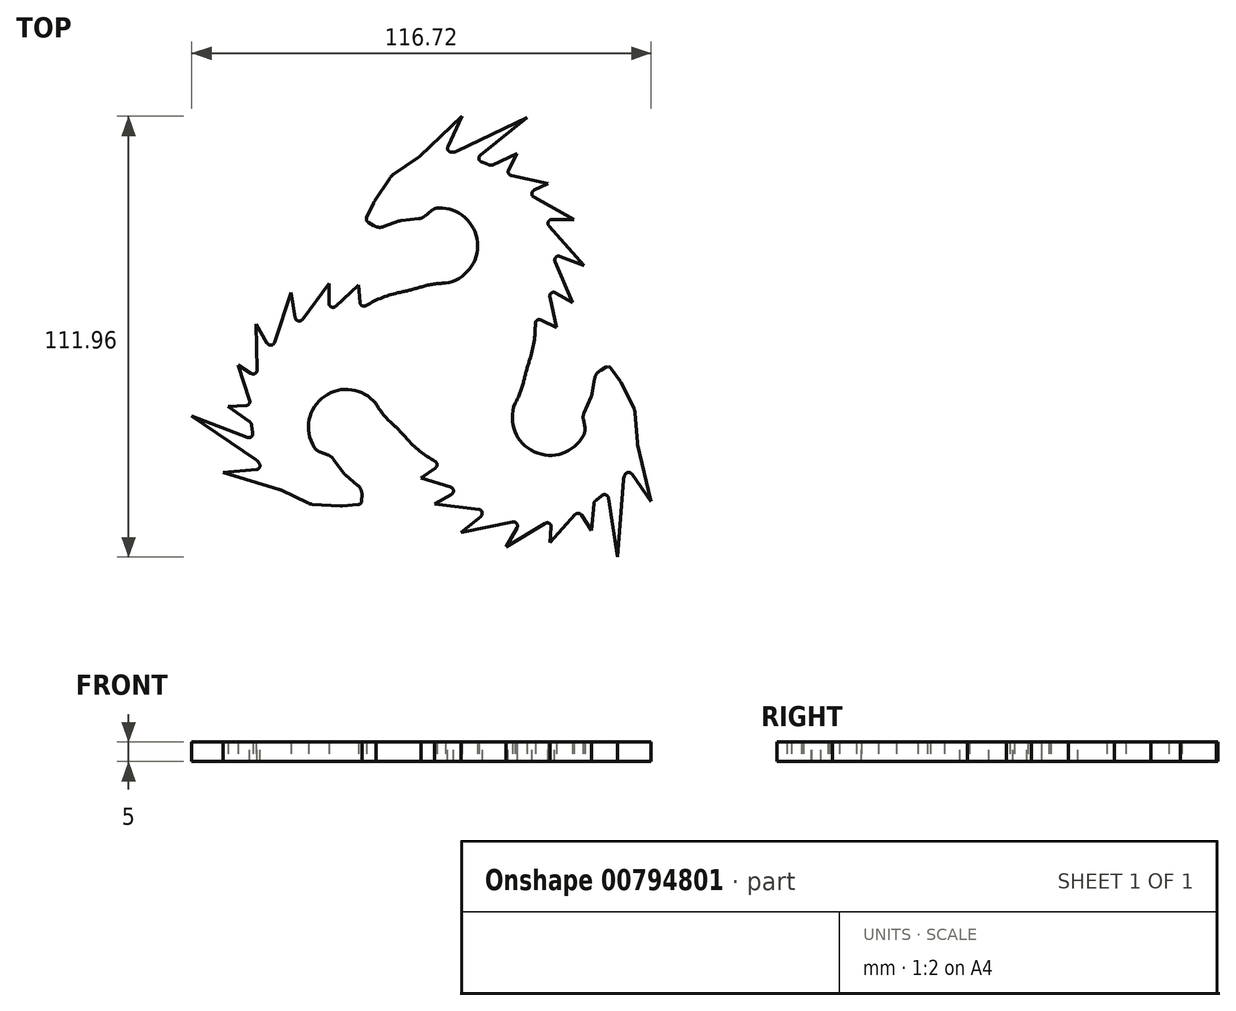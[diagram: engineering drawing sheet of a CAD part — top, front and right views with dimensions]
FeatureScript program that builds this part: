
annotation { "Feature Type Name" : "Feature", "Feature Type Description" : "" }
export const myFeature = defineFeature(function(context is Context, id is Id, definition is map)
    precondition{}
    {
        {
            var Q0;
            Q0=qCreatedBy(makeId("Top.planeOp"),FACE);
            var sketch = newSketch(context, id + "F0", { "sketchPlane" : qUnion([Q0])});
            skCircle(sketch, "E0", {"center": v(0, 0) * mm, "radius": 14.28 * mm});
            skCircle(sketch, "E1", {"center": v(0, 0) * mm, "radius": 20.4 * mm});
            skArc(sketch, "E2", {"start": v(0, 20.4) * mm, "mid": v(8.14, 30.78) * mm, "end": v(-1.75, 39.51) * mm});
            skArc(sketch, "E3", {"start": v(19.07, 7.24) * mm, "mid": v(26.13, 32.87) * mm, "end": v(7.42, 51.76) * mm});
            skLineSegment(sketch, "E4", {"start": v(7.42, 51.76) * mm, "end": v(20.67, 62.5) * mm});
            skLineSegment(sketch, "E5", {"start": v(20.67, 62.5) * mm, "end": v(2.99, 53.95) * mm});
            skLineSegment(sketch, "E6", {"start": v(1.68, 53.66) * mm, "end": v(0, 53.66) * mm});
            skLineSegment(sketch, "E7", {"start": v(-6.98, 52.26) * mm, "end": v(-13.25, 47.99) * mm});
            skLineSegment(sketch, "E8", {"start": v(-20.36, 36.3) * mm, "end": v(-18.24, 40.82) * mm});
            skLineSegment(sketch, "E9", {"start": v(-18.02, 41.22) * mm, "end": v(-14.05, 47.17) * mm});
            skLineSegment(sketch, "E10", {"start": v(-3.58, 38.81) * mm, "end": v(-5.17, 37.47) * mm});
            skLineSegment(sketch, "E11", {"start": v(-6.77, 36.79) * mm, "end": v(-11.2, 36.3) * mm});
            skLineSegment(sketch, "E12", {"start": v(-11.89, 36.13) * mm, "end": v(-15.65, 34.77) * mm});
            skLineSegment(sketch, "E13", {"start": v(-18.22, 35.01) * mm, "end": v(-20.36, 36.3) * mm});
            skLineSegment(sketch, "E14", {"start": v(0, 53.66) * mm, "end": v(4.26, 62.8) * mm});
            skLineSegment(sketch, "E15", {"start": v(4.26, 62.8) * mm, "end": v(-6.61, 52.56) * mm});
            skLineSegment(sketch, "E16", {"start": v(15.49, 48.02) * mm, "end": v(26.04, 45.77) * mm});
            skLineSegment(sketch, "E17", {"start": v(26.04, 45.77) * mm, "end": v(20.8, 43.18) * mm});
            skLineSegment(sketch, "E18", {"start": v(20.8, 43.18) * mm, "end": v(32.67, 36.61) * mm});
            skLineSegment(sketch, "E19", {"start": v(32.67, 36.61) * mm, "end": v(24.84, 36.61) * mm});
            skLineSegment(sketch, "E20", {"start": v(24.84, 36.61) * mm, "end": v(35.2, 24.93) * mm});
            skLineSegment(sketch, "E21", {"start": v(35.2, 24.93) * mm, "end": v(26.92, 28.04) * mm});
            skLineSegment(sketch, "E22", {"start": v(26.92, 28.04) * mm, "end": v(32.35, 15.47) * mm});
            skLineSegment(sketch, "E23", {"start": v(32.35, 15.47) * mm, "end": v(26.04, 19.1) * mm});
            skLineSegment(sketch, "E24", {"start": v(26.04, 19.1) * mm, "end": v(28.25, 9.15) * mm});
            skLineSegment(sketch, "E25", {"start": v(28.25, 9.15) * mm, "end": v(22.76, 11.77) * mm});
            skLineSegment(sketch, "E26", {"start": v(11.52, 50.27) * mm, "end": v(18.15, 53.34) * mm});
            skPoint(sketch, "E26.startSnap0", {"position": v(11.52, 58.07) * mm});
            skLineSegment(sketch, "E27", {"start": v(18.15, 53.34) * mm, "end": v(15.49, 48.02) * mm});
            skPoint(sketch, "E28.visualSharp", {"position": v(-17, 34.28) * mm});
            skArc(sketch, "E28.filletArc", {"start": v(-18.22, 35.01) * mm, "mid": v(-16.96, 34.6) * mm, "end": v(-15.65, 34.77) * mm});
            skPoint(sketch, "E29.visualSharp", {"position": v(-11.55, 36.26) * mm});
            skArc(sketch, "E29.filletArc", {"start": v(-11.2, 36.3) * mm, "mid": v(-11.54, 36.24) * mm, "end": v(-11.89, 36.13) * mm});
            skPoint(sketch, "E30.visualSharp", {"position": v(-5.87, 36.89) * mm});
            skArc(sketch, "E30.filletArc", {"start": v(-6.77, 36.79) * mm, "mid": v(-5.92, 37.01) * mm, "end": v(-5.17, 37.47) * mm});
            skPoint(sketch, "E31.visualSharp", {"position": v(-2.87, 39.41) * mm});
            skArc(sketch, "E31.filletArc", {"start": v(-1.75, 39.51) * mm, "mid": v(-2.72, 39.32) * mm, "end": v(-3.58, 38.81) * mm});
            skPoint(sketch, "E32.visualSharp", {"position": v(-18.15, 41.03) * mm});
            skArc(sketch, "E32.filletArc", {"start": v(-18.02, 41.22) * mm, "mid": v(-18.14, 41.03) * mm, "end": v(-18.24, 40.82) * mm});
            skPoint(sketch, "E33.visualSharp", {"position": v(-13.73, 47.66) * mm});
            skArc(sketch, "E33.filletArc", {"start": v(-13.25, 47.99) * mm, "mid": v(-13.69, 47.62) * mm, "end": v(-14.05, 47.17) * mm});
            skPoint(sketch, "E34.visualSharp", {"position": v(-6.79, 52.4) * mm});
            skArc(sketch, "E34.filletArc", {"start": v(-6.98, 52.26) * mm, "mid": v(-6.8, 52.4) * mm, "end": v(-6.61, 52.56) * mm});
            skPoint(sketch, "E35.visualSharp", {"position": v(2.37, 53.66) * mm});
            skArc(sketch, "E35.filletArc", {"start": v(1.68, 53.66) * mm, "mid": v(2.35, 53.73) * mm, "end": v(2.99, 53.95) * mm});
            skArc(sketch, "E36", {"start": v(20.32, -1.85) * mm, "mid": v(22.4, 4.8) * mm, "end": v(22.76, 11.77) * mm});
            skSolve(sketch);
        }
        {
            var Q0;
            Q0=qSketchRegion(id+"F0",true);
            extrude(context, id + "F1", {"entities" : qUnion([Q0]), "depth" : 5 * mm, "offsetDistance" : 25 * mm});
        }
        {
            var Q0;
            Q0=makeQuery(id+"F1.opExtrude","SWEPT_EDGE",EDGE,{"disambiguationData":[OSD([sQuery(id+"F0.wireOp",EDGE,"E1"),sQuery(id+"F0.wireOp",EDGE,"E36")])]});
            fillet(context, id + "F2", {"entities" : qUnion([Q0]), "radius" : 55 * mm, "tangentPropagation" : true, "allowEdgeOverflow" : false});
        }
        {
            var Q0;
            Q0=makeQuery(id+"F1.opExtrude","SWEPT_EDGE",EDGE,{"disambiguationData":[OSD([sQuery(id+"F0.wireOp",EDGE,"E3"),sQuery(id+"F0.wireOp",EDGE,"E25"),sQuery(id+"F0.wireOp",EDGE,"E36")])]});
            var Q1;
            Q1=makeQuery(id+"F1.opExtrude","SWEPT_EDGE",EDGE,{"disambiguationData":[OSD([sQuery(id+"F0.wireOp",EDGE,"E3"),sQuery(id+"F0.wireOp",EDGE,"E23"),sQuery(id+"F0.wireOp",EDGE,"E24")])]});
            var Q2;
            Q2=makeQuery(id+"F1.opExtrude","SWEPT_EDGE",EDGE,{"disambiguationData":[OSD([sQuery(id+"F0.wireOp",EDGE,"E3"),sQuery(id+"F0.wireOp",EDGE,"E21"),sQuery(id+"F0.wireOp",EDGE,"E22")])]});
            var Q3;
            Q3=makeQuery(id+"F1.opExtrude","SWEPT_EDGE",EDGE,{"disambiguationData":[OSD([sQuery(id+"F0.wireOp",EDGE,"E3"),sQuery(id+"F0.wireOp",EDGE,"E19"),sQuery(id+"F0.wireOp",EDGE,"E20")])]});
            var Q4;
            Q4=makeQuery(id+"F1.opExtrude","SWEPT_EDGE",EDGE,{"disambiguationData":[OSD([sQuery(id+"F0.wireOp",EDGE,"E3"),sQuery(id+"F0.wireOp",EDGE,"E17"),sQuery(id+"F0.wireOp",EDGE,"E18")])]});
            var Q5;
            Q5=makeQuery(id+"F1.opExtrude","SWEPT_EDGE",EDGE,{"disambiguationData":[OSD([sQuery(id+"F0.wireOp",EDGE,"E3"),sQuery(id+"F0.wireOp",EDGE,"E16"),sQuery(id+"F0.wireOp",EDGE,"E27")])]});
            var Q6;
            Q6=makeQuery(id+"F1.opExtrude","SWEPT_EDGE",EDGE,{"disambiguationData":[OSD([sQuery(id+"F0.wireOp",EDGE,"E3"),sQuery(id+"F0.wireOp",EDGE,"E26")])]});
            var Q7;
            Q7=makeQuery(id+"F1.opExtrude","SWEPT_EDGE",EDGE,{"disambiguationData":[OSD([sQuery(id+"F0.wireOp",EDGE,"E3"),sQuery(id+"F0.wireOp",EDGE,"E4")])]});
            var Q8;
            Q8=makeQuery(id+"F1.opExtrude","SWEPT_EDGE",EDGE,{"disambiguationData":[OSD([sQuery(id+"F0.wireOp",EDGE,"E6"),sQuery(id+"F0.wireOp",EDGE,"E14")])]});
            fillet(context, id + "F3", {"entities" : qUnion([Q0, Q1, Q2, Q3, Q4, Q5, Q6, Q7, Q8]), "radius" : 1 * mm, "tangentPropagation" : true, "allowEdgeOverflow" : false});
        }
        {
            var Q0;
            Q0=makeQuery(id+"F1.opExtrude","SWEPT_EDGE",EDGE,{"disambiguationData":[OSD([sQuery(id+"F0.wireOp",EDGE,"E8"),sQuery(id+"F0.wireOp",EDGE,"E13")])]});
            fillet(context, id + "F4", {"entities" : qUnion([Q0]), "radius" : 1 * mm, "tangentPropagation" : true, "allowEdgeOverflow" : false});
        }
        {
            var Q0;
            Q0=makeQuery(id+"F1.opExtrude","SWEPT_BODY",BODY,{"disambiguationData":[OSD([sQuery(id+"F0.wireOp",EDGE,"E0"),sQuery(id+"F0.wireOp",EDGE,"E1"),sQuery(id+"F0.wireOp",EDGE,"E2"),sQuery(id+"F0.wireOp",EDGE,"E3"),sQuery(id+"F0.wireOp",EDGE,"E4"),sQuery(id+"F0.wireOp",EDGE,"E5"),sQuery(id+"F0.wireOp",EDGE,"E6"),sQuery(id+"F0.wireOp",EDGE,"E7"),sQuery(id+"F0.wireOp",EDGE,"E8"),sQuery(id+"F0.wireOp",EDGE,"E9"),sQuery(id+"F0.wireOp",EDGE,"E10"),sQuery(id+"F0.wireOp",EDGE,"E11"),sQuery(id+"F0.wireOp",EDGE,"E12"),sQuery(id+"F0.wireOp",EDGE,"E13"),sQuery(id+"F0.wireOp",EDGE,"E14"),sQuery(id+"F0.wireOp",EDGE,"E15"),sQuery(id+"F0.wireOp",EDGE,"E16"),sQuery(id+"F0.wireOp",EDGE,"E17"),sQuery(id+"F0.wireOp",EDGE,"E18"),sQuery(id+"F0.wireOp",EDGE,"E19"),sQuery(id+"F0.wireOp",EDGE,"E20"),sQuery(id+"F0.wireOp",EDGE,"E21"),sQuery(id+"F0.wireOp",EDGE,"E22"),sQuery(id+"F0.wireOp",EDGE,"E23"),sQuery(id+"F0.wireOp",EDGE,"E24"),sQuery(id+"F0.wireOp",EDGE,"E25"),sQuery(id+"F0.wireOp",EDGE,"E26"),sQuery(id+"F0.wireOp",EDGE,"E27"),sQuery(id+"F0.wireOp",EDGE,"E28.filletArc"),sQuery(id+"F0.wireOp",EDGE,"E29.filletArc"),sQuery(id+"F0.wireOp",EDGE,"E30.filletArc"),sQuery(id+"F0.wireOp",EDGE,"E31.filletArc"),sQuery(id+"F0.wireOp",EDGE,"E32.filletArc"),sQuery(id+"F0.wireOp",EDGE,"E33.filletArc"),sQuery(id+"F0.wireOp",EDGE,"E34.filletArc"),sQuery(id+"F0.wireOp",EDGE,"E35.filletArc"),sQuery(id+"F0.wireOp",EDGE,"E36")])]});
            var Q1;
            Q1=makeQuery(id+"F1.opExtrude","CAP_EDGE",EDGE,{"disambiguationData":[OSD([sQuery(id+"F0.wireOp",EDGE,"E0")])],"isStart":false});
            circularPattern(context, id + "F5", {"entities" : qUnion([Q0]), "axis" : qUnion([Q1]), "angle" : 360 * degree, "instanceCount" : 3, "equalSpace" : true, "isCentered" : true});
        }
        {
            var Q0;
            Q0=makeQuery(id+"F1.opExtrude","SWEPT_BODY",BODY,{"disambiguationData":[OSD([sQuery(id+"F0.wireOp",EDGE,"E0"),sQuery(id+"F0.wireOp",EDGE,"E1"),sQuery(id+"F0.wireOp",EDGE,"E2"),sQuery(id+"F0.wireOp",EDGE,"E3"),sQuery(id+"F0.wireOp",EDGE,"E4"),sQuery(id+"F0.wireOp",EDGE,"E5"),sQuery(id+"F0.wireOp",EDGE,"E6"),sQuery(id+"F0.wireOp",EDGE,"E7"),sQuery(id+"F0.wireOp",EDGE,"E8"),sQuery(id+"F0.wireOp",EDGE,"E9"),sQuery(id+"F0.wireOp",EDGE,"E10"),sQuery(id+"F0.wireOp",EDGE,"E11"),sQuery(id+"F0.wireOp",EDGE,"E12"),sQuery(id+"F0.wireOp",EDGE,"E13"),sQuery(id+"F0.wireOp",EDGE,"E14"),sQuery(id+"F0.wireOp",EDGE,"E15"),sQuery(id+"F0.wireOp",EDGE,"E16"),sQuery(id+"F0.wireOp",EDGE,"E17"),sQuery(id+"F0.wireOp",EDGE,"E18"),sQuery(id+"F0.wireOp",EDGE,"E19"),sQuery(id+"F0.wireOp",EDGE,"E20"),sQuery(id+"F0.wireOp",EDGE,"E21"),sQuery(id+"F0.wireOp",EDGE,"E22"),sQuery(id+"F0.wireOp",EDGE,"E23"),sQuery(id+"F0.wireOp",EDGE,"E24"),sQuery(id+"F0.wireOp",EDGE,"E25"),sQuery(id+"F0.wireOp",EDGE,"E26"),sQuery(id+"F0.wireOp",EDGE,"E27"),sQuery(id+"F0.wireOp",EDGE,"E28.filletArc"),sQuery(id+"F0.wireOp",EDGE,"E29.filletArc"),sQuery(id+"F0.wireOp",EDGE,"E30.filletArc"),sQuery(id+"F0.wireOp",EDGE,"E31.filletArc"),sQuery(id+"F0.wireOp",EDGE,"E32.filletArc"),sQuery(id+"F0.wireOp",EDGE,"E33.filletArc"),sQuery(id+"F0.wireOp",EDGE,"E34.filletArc"),sQuery(id+"F0.wireOp",EDGE,"E35.filletArc"),sQuery(id+"F0.wireOp",EDGE,"E36")])]});
            var Q1;
            Q1=makeQuery(id+"F5.opPattern","COPY",BODY,{"derivedFrom":makeQuery(id+"F1.opExtrude","SWEPT_BODY",BODY,{"disambiguationData":[OSD([sQuery(id+"F0.wireOp",EDGE,"E0"),sQuery(id+"F0.wireOp",EDGE,"E1"),sQuery(id+"F0.wireOp",EDGE,"E2"),sQuery(id+"F0.wireOp",EDGE,"E3"),sQuery(id+"F0.wireOp",EDGE,"E4"),sQuery(id+"F0.wireOp",EDGE,"E5"),sQuery(id+"F0.wireOp",EDGE,"E6"),sQuery(id+"F0.wireOp",EDGE,"E7"),sQuery(id+"F0.wireOp",EDGE,"E8"),sQuery(id+"F0.wireOp",EDGE,"E9"),sQuery(id+"F0.wireOp",EDGE,"E10"),sQuery(id+"F0.wireOp",EDGE,"E11"),sQuery(id+"F0.wireOp",EDGE,"E12"),sQuery(id+"F0.wireOp",EDGE,"E13"),sQuery(id+"F0.wireOp",EDGE,"E14"),sQuery(id+"F0.wireOp",EDGE,"E15"),sQuery(id+"F0.wireOp",EDGE,"E16"),sQuery(id+"F0.wireOp",EDGE,"E17"),sQuery(id+"F0.wireOp",EDGE,"E18"),sQuery(id+"F0.wireOp",EDGE,"E19"),sQuery(id+"F0.wireOp",EDGE,"E20"),sQuery(id+"F0.wireOp",EDGE,"E21"),sQuery(id+"F0.wireOp",EDGE,"E22"),sQuery(id+"F0.wireOp",EDGE,"E23"),sQuery(id+"F0.wireOp",EDGE,"E24"),sQuery(id+"F0.wireOp",EDGE,"E25"),sQuery(id+"F0.wireOp",EDGE,"E26"),sQuery(id+"F0.wireOp",EDGE,"E27"),sQuery(id+"F0.wireOp",EDGE,"E28.filletArc"),sQuery(id+"F0.wireOp",EDGE,"E29.filletArc"),sQuery(id+"F0.wireOp",EDGE,"E30.filletArc"),sQuery(id+"F0.wireOp",EDGE,"E31.filletArc"),sQuery(id+"F0.wireOp",EDGE,"E32.filletArc"),sQuery(id+"F0.wireOp",EDGE,"E33.filletArc"),sQuery(id+"F0.wireOp",EDGE,"E34.filletArc"),sQuery(id+"F0.wireOp",EDGE,"E35.filletArc"),sQuery(id+"F0.wireOp",EDGE,"E36")])]}),"instanceName":"-2"});
            var Q2;
            Q2=makeQuery(id+"F5.opPattern","COPY",BODY,{"derivedFrom":makeQuery(id+"F1.opExtrude","SWEPT_BODY",BODY,{"disambiguationData":[OSD([sQuery(id+"F0.wireOp",EDGE,"E0"),sQuery(id+"F0.wireOp",EDGE,"E1"),sQuery(id+"F0.wireOp",EDGE,"E2"),sQuery(id+"F0.wireOp",EDGE,"E3"),sQuery(id+"F0.wireOp",EDGE,"E4"),sQuery(id+"F0.wireOp",EDGE,"E5"),sQuery(id+"F0.wireOp",EDGE,"E6"),sQuery(id+"F0.wireOp",EDGE,"E7"),sQuery(id+"F0.wireOp",EDGE,"E8"),sQuery(id+"F0.wireOp",EDGE,"E9"),sQuery(id+"F0.wireOp",EDGE,"E10"),sQuery(id+"F0.wireOp",EDGE,"E11"),sQuery(id+"F0.wireOp",EDGE,"E12"),sQuery(id+"F0.wireOp",EDGE,"E13"),sQuery(id+"F0.wireOp",EDGE,"E14"),sQuery(id+"F0.wireOp",EDGE,"E15"),sQuery(id+"F0.wireOp",EDGE,"E16"),sQuery(id+"F0.wireOp",EDGE,"E17"),sQuery(id+"F0.wireOp",EDGE,"E18"),sQuery(id+"F0.wireOp",EDGE,"E19"),sQuery(id+"F0.wireOp",EDGE,"E20"),sQuery(id+"F0.wireOp",EDGE,"E21"),sQuery(id+"F0.wireOp",EDGE,"E22"),sQuery(id+"F0.wireOp",EDGE,"E23"),sQuery(id+"F0.wireOp",EDGE,"E24"),sQuery(id+"F0.wireOp",EDGE,"E25"),sQuery(id+"F0.wireOp",EDGE,"E26"),sQuery(id+"F0.wireOp",EDGE,"E27"),sQuery(id+"F0.wireOp",EDGE,"E28.filletArc"),sQuery(id+"F0.wireOp",EDGE,"E29.filletArc"),sQuery(id+"F0.wireOp",EDGE,"E30.filletArc"),sQuery(id+"F0.wireOp",EDGE,"E31.filletArc"),sQuery(id+"F0.wireOp",EDGE,"E32.filletArc"),sQuery(id+"F0.wireOp",EDGE,"E33.filletArc"),sQuery(id+"F0.wireOp",EDGE,"E34.filletArc"),sQuery(id+"F0.wireOp",EDGE,"E35.filletArc"),sQuery(id+"F0.wireOp",EDGE,"E36")])]}),"instanceName":"-1"});
            var Q3;
            Q3=makeQuery(id+"F5.opPattern","COPY",BODY,{"derivedFrom":makeQuery(id+"F1.opExtrude","SWEPT_BODY",BODY,{"disambiguationData":[OSD([sQuery(id+"F0.wireOp",EDGE,"E0"),sQuery(id+"F0.wireOp",EDGE,"E1"),sQuery(id+"F0.wireOp",EDGE,"E2"),sQuery(id+"F0.wireOp",EDGE,"E3"),sQuery(id+"F0.wireOp",EDGE,"E4"),sQuery(id+"F0.wireOp",EDGE,"E5"),sQuery(id+"F0.wireOp",EDGE,"E6"),sQuery(id+"F0.wireOp",EDGE,"E7"),sQuery(id+"F0.wireOp",EDGE,"E8"),sQuery(id+"F0.wireOp",EDGE,"E9"),sQuery(id+"F0.wireOp",EDGE,"E10"),sQuery(id+"F0.wireOp",EDGE,"E11"),sQuery(id+"F0.wireOp",EDGE,"E12"),sQuery(id+"F0.wireOp",EDGE,"E13"),sQuery(id+"F0.wireOp",EDGE,"E14"),sQuery(id+"F0.wireOp",EDGE,"E15"),sQuery(id+"F0.wireOp",EDGE,"E16"),sQuery(id+"F0.wireOp",EDGE,"E17"),sQuery(id+"F0.wireOp",EDGE,"E18"),sQuery(id+"F0.wireOp",EDGE,"E19"),sQuery(id+"F0.wireOp",EDGE,"E20"),sQuery(id+"F0.wireOp",EDGE,"E21"),sQuery(id+"F0.wireOp",EDGE,"E22"),sQuery(id+"F0.wireOp",EDGE,"E23"),sQuery(id+"F0.wireOp",EDGE,"E24"),sQuery(id+"F0.wireOp",EDGE,"E25"),sQuery(id+"F0.wireOp",EDGE,"E26"),sQuery(id+"F0.wireOp",EDGE,"E27"),sQuery(id+"F0.wireOp",EDGE,"E28.filletArc"),sQuery(id+"F0.wireOp",EDGE,"E29.filletArc"),sQuery(id+"F0.wireOp",EDGE,"E30.filletArc"),sQuery(id+"F0.wireOp",EDGE,"E31.filletArc"),sQuery(id+"F0.wireOp",EDGE,"E32.filletArc"),sQuery(id+"F0.wireOp",EDGE,"E33.filletArc"),sQuery(id+"F0.wireOp",EDGE,"E34.filletArc"),sQuery(id+"F0.wireOp",EDGE,"E35.filletArc"),sQuery(id+"F0.wireOp",EDGE,"E36")])]}),"instanceName":"1"});
            var Q4;
            Q4=makeQuery(id+"F5.opPattern","COPY",BODY,{"derivedFrom":makeQuery(id+"F1.opExtrude","SWEPT_BODY",BODY,{"disambiguationData":[OSD([sQuery(id+"F0.wireOp",EDGE,"E0"),sQuery(id+"F0.wireOp",EDGE,"E1"),sQuery(id+"F0.wireOp",EDGE,"E2"),sQuery(id+"F0.wireOp",EDGE,"E3"),sQuery(id+"F0.wireOp",EDGE,"E4"),sQuery(id+"F0.wireOp",EDGE,"E5"),sQuery(id+"F0.wireOp",EDGE,"E6"),sQuery(id+"F0.wireOp",EDGE,"E7"),sQuery(id+"F0.wireOp",EDGE,"E8"),sQuery(id+"F0.wireOp",EDGE,"E9"),sQuery(id+"F0.wireOp",EDGE,"E10"),sQuery(id+"F0.wireOp",EDGE,"E11"),sQuery(id+"F0.wireOp",EDGE,"E12"),sQuery(id+"F0.wireOp",EDGE,"E13"),sQuery(id+"F0.wireOp",EDGE,"E14"),sQuery(id+"F0.wireOp",EDGE,"E15"),sQuery(id+"F0.wireOp",EDGE,"E16"),sQuery(id+"F0.wireOp",EDGE,"E17"),sQuery(id+"F0.wireOp",EDGE,"E18"),sQuery(id+"F0.wireOp",EDGE,"E19"),sQuery(id+"F0.wireOp",EDGE,"E20"),sQuery(id+"F0.wireOp",EDGE,"E21"),sQuery(id+"F0.wireOp",EDGE,"E22"),sQuery(id+"F0.wireOp",EDGE,"E23"),sQuery(id+"F0.wireOp",EDGE,"E24"),sQuery(id+"F0.wireOp",EDGE,"E25"),sQuery(id+"F0.wireOp",EDGE,"E26"),sQuery(id+"F0.wireOp",EDGE,"E27"),sQuery(id+"F0.wireOp",EDGE,"E28.filletArc"),sQuery(id+"F0.wireOp",EDGE,"E29.filletArc"),sQuery(id+"F0.wireOp",EDGE,"E30.filletArc"),sQuery(id+"F0.wireOp",EDGE,"E31.filletArc"),sQuery(id+"F0.wireOp",EDGE,"E32.filletArc"),sQuery(id+"F0.wireOp",EDGE,"E33.filletArc"),sQuery(id+"F0.wireOp",EDGE,"E34.filletArc"),sQuery(id+"F0.wireOp",EDGE,"E35.filletArc"),sQuery(id+"F0.wireOp",EDGE,"E36")])]}),"instanceName":"2"});
            booleanBodies(context, id + "F6", {"operationType" : BooleanOperationType.UNION, "tools" : qUnion([Q0, Q1, Q2, Q3, Q4])});
        }
        {
            var Q0;
            {var subQ0=makeQuery(id+"F1.opExtrude","CAP_FACE",FACE,{"disambiguationData":[OSD([sQuery(id+"F0.wireOp",EDGE,"E0"),sQuery(id+"F0.wireOp",EDGE,"E1"),sQuery(id+"F0.wireOp",EDGE,"E2"),sQuery(id+"F0.wireOp",EDGE,"E3"),sQuery(id+"F0.wireOp",EDGE,"E4"),sQuery(id+"F0.wireOp",EDGE,"E5"),sQuery(id+"F0.wireOp",EDGE,"E6"),sQuery(id+"F0.wireOp",EDGE,"E7"),sQuery(id+"F0.wireOp",EDGE,"E8"),sQuery(id+"F0.wireOp",EDGE,"E9"),sQuery(id+"F0.wireOp",EDGE,"E10"),sQuery(id+"F0.wireOp",EDGE,"E11"),sQuery(id+"F0.wireOp",EDGE,"E12"),sQuery(id+"F0.wireOp",EDGE,"E13"),sQuery(id+"F0.wireOp",EDGE,"E14"),sQuery(id+"F0.wireOp",EDGE,"E15"),sQuery(id+"F0.wireOp",EDGE,"E16"),sQuery(id+"F0.wireOp",EDGE,"E17"),sQuery(id+"F0.wireOp",EDGE,"E18"),sQuery(id+"F0.wireOp",EDGE,"E19"),sQuery(id+"F0.wireOp",EDGE,"E20"),sQuery(id+"F0.wireOp",EDGE,"E21"),sQuery(id+"F0.wireOp",EDGE,"E22"),sQuery(id+"F0.wireOp",EDGE,"E23"),sQuery(id+"F0.wireOp",EDGE,"E24"),sQuery(id+"F0.wireOp",EDGE,"E25"),sQuery(id+"F0.wireOp",EDGE,"E26"),sQuery(id+"F0.wireOp",EDGE,"E27"),sQuery(id+"F0.wireOp",EDGE,"E28.filletArc"),sQuery(id+"F0.wireOp",EDGE,"E29.filletArc"),sQuery(id+"F0.wireOp",EDGE,"E30.filletArc"),sQuery(id+"F0.wireOp",EDGE,"E31.filletArc"),sQuery(id+"F0.wireOp",EDGE,"E32.filletArc"),sQuery(id+"F0.wireOp",EDGE,"E33.filletArc"),sQuery(id+"F0.wireOp",EDGE,"E34.filletArc"),sQuery(id+"F0.wireOp",EDGE,"E35.filletArc"),sQuery(id+"F0.wireOp",EDGE,"E36")])],"isStart":false});Q0=makeQuery(id+"F6.opBoolean","MERGE",FACE,{"derivedFrom":[subQ0,makeQuery(id+"F5.opPattern","COPY",FACE,{"derivedFrom":subQ0,"instanceName":"-2"}),makeQuery(id+"F5.opPattern","COPY",FACE,{"derivedFrom":subQ0,"instanceName":"-1"}),makeQuery(id+"F5.opPattern","COPY",FACE,{"derivedFrom":subQ0,"instanceName":"1"}),makeQuery(id+"F5.opPattern","COPY",FACE,{"derivedFrom":subQ0,"instanceName":"2"})]});}
            var sketch = newSketch(context, id + "F7", { "sketchPlane" : qUnion([Q0])});
            skCircle(sketch, "E37.0", {"center": v(0, 0) * mm, "radius": 14.28 * mm});
            skSolve(sketch);
        }
        {
            var Q0;
            Q0 = qSketchRegion(id + "F7", true);
            extrude(context, id + "F8", {"entities" : qUnion([Q0]), "operationType" : NewBodyOperationType.ADD, "oppositeDirection" : true, "depth" : 5 * mm, "offsetDistance" : 25 * mm});
        }
    });
